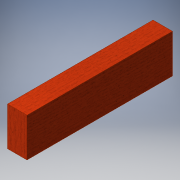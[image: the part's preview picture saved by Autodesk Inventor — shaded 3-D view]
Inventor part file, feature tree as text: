
AUTODESK INVENTOR PART (.ipt)
format: ipt  version: 2016 (Build 200138000, 138)  size: 102,400 bytes
history: native  units: in
note: dims shown in document units (in); Inventor stores cm internally (conversion verified against a paired STEP export)
features: extrude x1, sketch x1
ambient origin geometry x8: Origin, YZ Plane, XZ Plane, XY Plane, X Axis, Y Axis, Z Axis, Center Point
bodies: Solid1 (feature_tree)
feature tree (2):
  extrude  "Extrusion1"  Depth=4.0in
  sketch  "Sketch1"  dims[d0=2.0in d1=4.0in d2=15.0in d3=0.0in]
